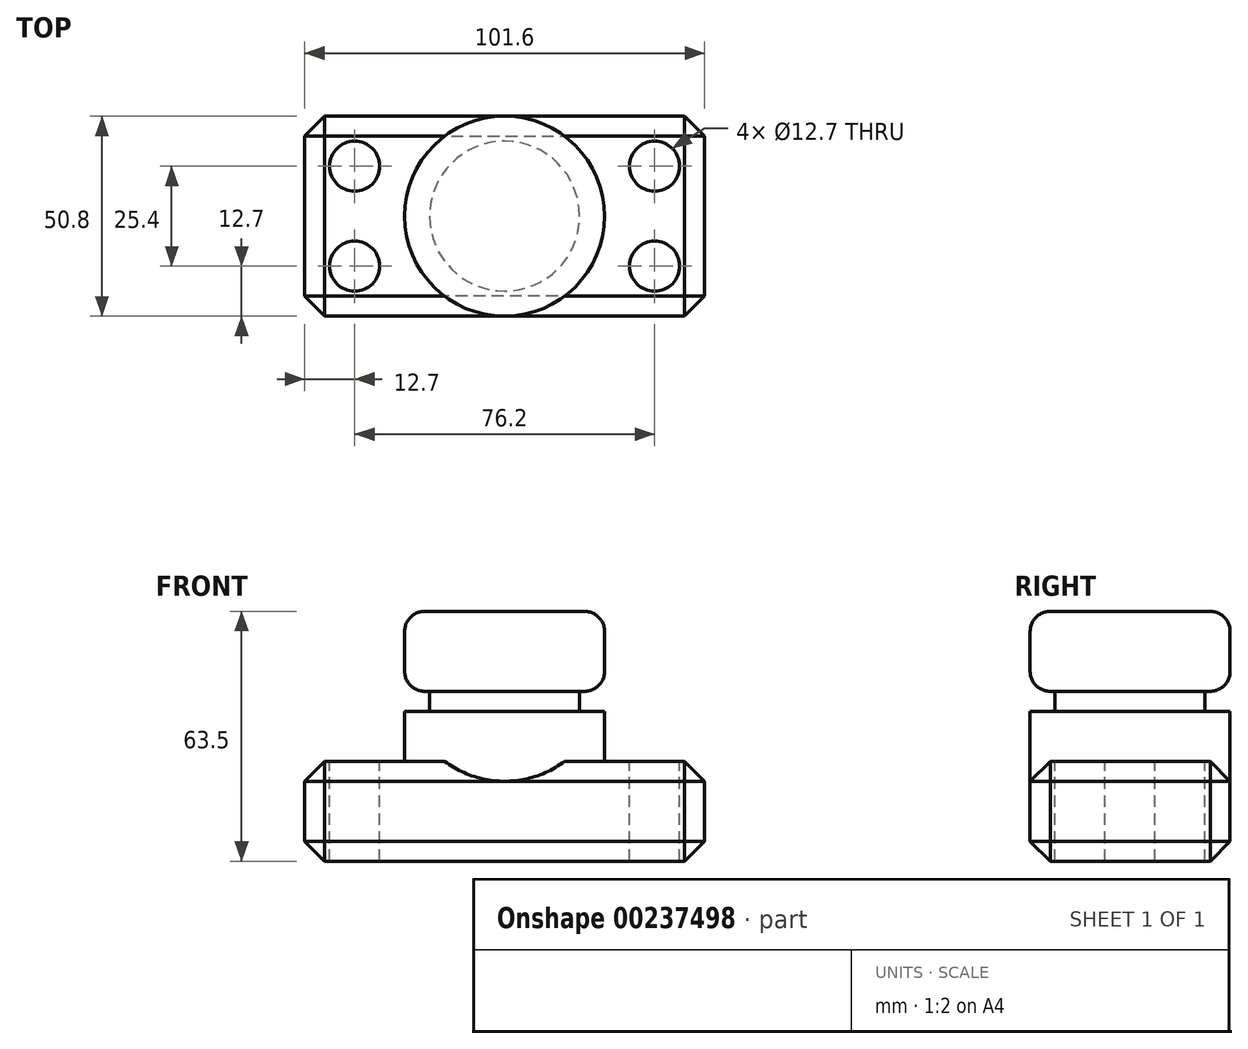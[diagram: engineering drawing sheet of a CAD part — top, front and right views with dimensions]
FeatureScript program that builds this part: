
annotation { "Feature Type Name" : "Feature", "Feature Type Description" : "" }
export const myFeature = defineFeature(function(context is Context, id is Id, definition is map)
    precondition{}
    {
        {
            var Q0;
            Q0=qCreatedBy(makeId("Top.planeOp"),FACE);
            var sketch = newSketch(context, id + "F0", { "sketchPlane" : qUnion([Q0])});
            skLineSegment(sketch, "E0.bottom", {"start": v(-50.8, 25.4) * mm, "end": v(50.8, 25.4) * mm});
            skLineSegment(sketch, "E0.top", {"start": v(-50.8, -25.4) * mm, "end": v(50.8, -25.4) * mm});
            skLineSegment(sketch, "E0.left", {"start": v(-50.8, 25.4) * mm, "end": v(-50.8, -25.4) * mm});
            skLineSegment(sketch, "E0.right", {"start": v(50.8, 25.4) * mm, "end": v(50.8, -25.4) * mm});
            skPoint(sketch, "E0.middle", {"position": v(0, 0) * mm});
            skSolve(sketch);
        }
        {
            var Q0;
            Q0=makeQuery(id+"F0.imprint","IMPRINT",FACE,{"disambiguationData":[TD([[makeQuery(id+"F0.imprint","IMPRINT",EDGE,{"derivedFrom":sQuery(id+"F0.wireOp",EDGE,"E0.bottom")}),-1.0]])]});
            extrude(context, id + "F1", {"entities" : qUnion([Q0]), "depth" : 25.4 * mm});
        }
        {
            var Q0;
            Q0=makeQuery(id+"F1.opExtrude","CAP_FACE",FACE,{"disambiguationData":[OSD([sQuery(id+"F0.wireOp",EDGE,"E0.bottom"),sQuery(id+"F0.wireOp",EDGE,"E0.top"),sQuery(id+"F0.wireOp",EDGE,"E0.left"),sQuery(id+"F0.wireOp",EDGE,"E0.right")])],"isStart":false});
            var sketch = newSketch(context, id + "F2", { "sketchPlane" : qUnion([Q0])});
            skCircle(sketch, "E1", {"center": v(-38.1, 12.7) * mm, "radius": 6.35 * mm});
            skCircle(sketch, "E2", {"center": v(38.1, 12.7) * mm, "radius": 6.35 * mm});
            skCircle(sketch, "E3", {"center": v(38.1, -12.7) * mm, "radius": 6.35 * mm});
            skCircle(sketch, "E4", {"center": v(-38.1, -12.7) * mm, "radius": 6.35 * mm});
            skSolve(sketch);
        }
        {
            var Q0;
            Q0=makeQuery(id+"F2.imprint","IMPRINT",FACE,{"disambiguationData":[TD([[makeQuery(id+"F2.imprint","IMPRINT",EDGE,{"derivedFrom":sQuery(id+"F2.wireOp",EDGE,"E1")}),1.0]])]});
            var Q1;
            Q1=makeQuery(id+"F2.imprint","IMPRINT",FACE,{"disambiguationData":[TD([[makeQuery(id+"F2.imprint","IMPRINT",EDGE,{"derivedFrom":sQuery(id+"F2.wireOp",EDGE,"E2")}),1.0]])]});
            var Q2;
            Q2=makeQuery(id+"F2.imprint","IMPRINT",FACE,{"disambiguationData":[TD([[makeQuery(id+"F2.imprint","IMPRINT",EDGE,{"derivedFrom":sQuery(id+"F2.wireOp",EDGE,"E3")}),1.0]])]});
            var Q3;
            Q3=makeQuery(id+"F2.imprint","IMPRINT",FACE,{"disambiguationData":[TD([[makeQuery(id+"F2.imprint","IMPRINT",EDGE,{"derivedFrom":sQuery(id+"F2.wireOp",EDGE,"E4")}),1.0]])]});
            extrude(context, id + "F3", {"entities" : qUnion([Q0, Q1, Q2, Q3]), "operationType" : NewBodyOperationType.REMOVE, "endBound" : BoundingType.THROUGH_ALL, "oppositeDirection" : true, "depth" : 25.4 * mm});
        }
        {
            var Q0;
            Q0=qCreatedBy(makeId("Front.planeOp"),FACE);
            var sketch = newSketch(context, id + "F4", { "sketchPlane" : qUnion([Q0])});
            skLineSegment(sketch, "E5.bottom", {"start": v(0, 25.4) * mm, "end": v(-25.4, 25.4) * mm});
            skLineSegment(sketch, "E5.top", {"start": v(0, 63.5) * mm, "end": v(-25.4, 63.5) * mm});
            skLineSegment(sketch, "E5.left", {"start": v(0, 25.4) * mm, "end": v(0, 63.5) * mm});
            skLineSegment(sketch, "E5.right", {"start": v(-25.4, 25.4) * mm, "end": v(-25.4, 63.5) * mm});
            skSolve(sketch);
        }
        {
            var Q0;
            Q0=makeQuery(id+"F4.imprint","IMPRINT",FACE,{"disambiguationData":[TD([[makeQuery(id+"F4.imprint","IMPRINT",EDGE,{"derivedFrom":sQuery(id+"F4.wireOp",EDGE,"E5.bottom")}),-1.0]])]});
            var Q1;
            Q1=sQuery(id+"F4.wireOp",EDGE,"E5.left");
            revolve(context, id + "F5", {"operationType" : NewBodyOperationType.ADD, "entities" : qUnion([Q0]), "axis" : qUnion([Q1]), "revolveType" : RevolveType.FULL});
        }
        {
            var Q0;
            Q0=qCreatedBy(makeId("Front.planeOp"),FACE);
            var sketch = newSketch(context, id + "F6", { "sketchPlane" : qUnion([Q0])});
            skLineSegment(sketch, "E6.bottom", {"start": v(-43.58, 38.1) * mm, "end": v(-19.05, 38.1) * mm});
            skLineSegment(sketch, "E6.top", {"start": v(-43.58, 43.18) * mm, "end": v(-19.05, 43.18) * mm});
            skLineSegment(sketch, "E6.left", {"start": v(-43.58, 38.1) * mm, "end": v(-43.58, 43.18) * mm});
            skLineSegment(sketch, "E6.right", {"start": v(-19.05, 38.1) * mm, "end": v(-19.05, 43.18) * mm});
            skPoint(sketch, "E6.middle", {"position": v(-31.32, 40.64) * mm});
            skSolve(sketch);
        }
        {
            var Q0;
            Q0=makeQuery(id+"F6.imprint","IMPRINT",FACE,{"disambiguationData":[TD([[makeQuery(id+"F6.imprint","IMPRINT",EDGE,{"derivedFrom":sQuery(id+"F6.wireOp",EDGE,"E6.bottom")}),1.0]])]});
            var Q1;
            Q1=makeQuery(id+"F5.opRevolve","SWEPT_FACE",FACE,{"disambiguationData":[OSD([sQuery(id+"F4.wireOp",EDGE,"E5.right")])]});
            revolve(context, id + "F7", {"operationType" : NewBodyOperationType.REMOVE, "entities" : qUnion([Q0]), "axis" : qUnion([Q1]), "revolveType" : RevolveType.FULL, "oppositeDirection" : true});
        }
        {
            var Q0;
            Q0=makeQuery(id+"F7.boolean.opBoolean","SPLIT",FACE,{"disambiguationData":[TD([makeQuery(id+"F5.opRevolve","SWEPT_FACE",FACE,{"disambiguationData":[OSD([sQuery(id+"F4.wireOp",EDGE,"E5.top")])]})])],"derivedFrom":makeQuery(id+"F5.opRevolve","SWEPT_FACE",FACE,{"disambiguationData":[OSD([sQuery(id+"F4.wireOp",EDGE,"E5.right")])]})});
            fillet(context, id + "F8", {"entities" : qUnion([Q0]), "radius" : 5.08 * mm, "tangentPropagation" : true, "allowEdgeOverflow" : false});
        }
        {
            var Q0;
            Q0=makeQuery(id+"F1.opExtrude","SWEPT_FACE",FACE,{"disambiguationData":[OSD([sQuery(id+"F0.wireOp",EDGE,"E0.top")])]});
            var Q1;
            Q1=makeQuery(id+"F1.opExtrude","SWEPT_FACE",FACE,{"disambiguationData":[OSD([sQuery(id+"F0.wireOp",EDGE,"E0.right")])]});
            var Q2;
            Q2=makeQuery(id+"F1.opExtrude","SWEPT_FACE",FACE,{"disambiguationData":[OSD([sQuery(id+"F0.wireOp",EDGE,"E0.bottom")])]});
            var Q3;
            Q3=makeQuery(id+"F1.opExtrude","SWEPT_FACE",FACE,{"disambiguationData":[OSD([sQuery(id+"F0.wireOp",EDGE,"E0.left")])]});
            chamfer(context, id + "F9", {"entities" : qUnion([Q0, Q1, Q2, Q3]), "width" : 5.08 * mm, "tangentPropagation" : true});
        }
    });
